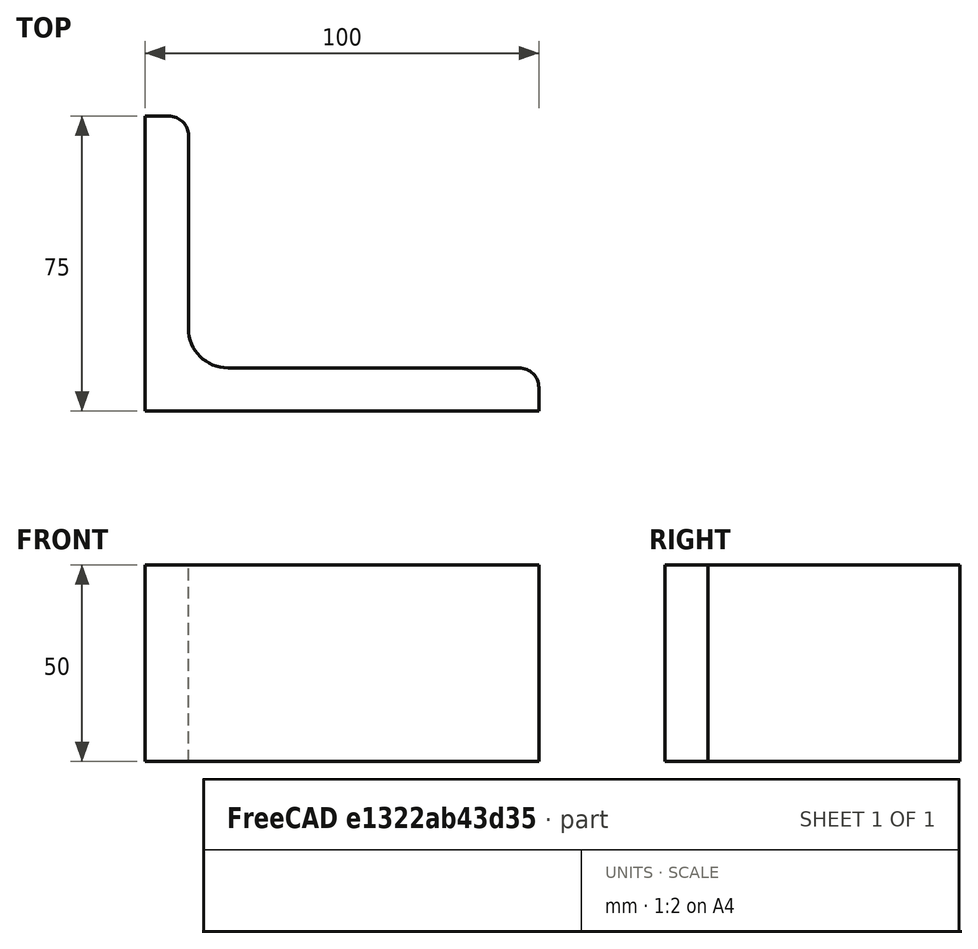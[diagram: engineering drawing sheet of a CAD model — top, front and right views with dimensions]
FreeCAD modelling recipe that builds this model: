
FCSTD DOCUMENT  (FreeCAD 0.15R4671 (Git))
Label: Angle Bar 100x75x11 EN10056 S235JR
License: All rights reserved
LicenseURL: http://en.wikipedia.org/wiki/All_rights_reserved
objects: Sketcher::SketchObject×1, Part::Extrusion×1
note: 2 computed .brp shape members not serialized (recipe doc carries the construction recipe); baked Part::Feature solids carry a one-line shape summary decoded from their .brp

FEATURE [Sketcher::SketchObject] Sketch
  sketch-geometry (9):
    g0: LineSegment StartX=0 StartY=0 StartZ=0 EndX=100 EndY=0 EndZ=0
    g1: LineSegment StartX=100 StartY=0 StartZ=0 EndX=100 EndY=6 EndZ=0
    g2: LineSegment StartX=95 StartY=11 StartZ=0 EndX=21 EndY=11 EndZ=0
    g3: LineSegment StartX=0 StartY=0 StartZ=0 EndX=0 EndY=75 EndZ=0
    g4: LineSegment StartX=0 StartY=75 StartZ=0 EndX=6 EndY=75 EndZ=0
    g5: LineSegment StartX=11 StartY=70 StartZ=0 EndX=11 EndY=21 EndZ=0
    g6: ArcOfCircle CenterX=21 CenterY=21 CenterZ=0 NormalX=0 NormalY=0 NormalZ=1 Radius=10 StartAngle=3.14159 EndAngle=4.71239
    g7: ArcOfCircle CenterX=6 CenterY=70 CenterZ=0 NormalX=0 NormalY=0 NormalZ=1 Radius=5 StartAngle=0 EndAngle=1.5708
    g8: ArcOfCircle CenterX=95 CenterY=6 CenterZ=0 NormalX=0 NormalY=0 NormalZ=1 Radius=5 StartAngle=0 EndAngle=1.5708
  constraints (23):
    c: Coincident(g0,g-1)
    c: Horizontal(g0)
    c: Coincident(g1,g0)
    c: Vertical(g1)
    c: Horizontal(g2)
    c: Coincident(g3,g-1)
    c: Vertical(g3)
    c: Coincident(g4,g3)
    c: Horizontal(g4)
    c: Vertical(g5)
    c: Tangent(g5,g6) = -1.5708
    c: Tangent(g2,g6) = 1.5708
    c: Tangent(g4,g7) = 1.5708
    c: Tangent(g5,g7) = 1.5708
    c: Tangent(g2,g8) = -1.5708
    c: Tangent(g1,g8) = -1.5708
    c: DistanceX(g0) = 100
    c: DistanceY(g3) = 75
    c: DistanceY(g0,g2) = 11
    c: DistanceX(g3,g5) = 11
    c: Radius(g6) = 10
    c: Radius(g8) = 5
    c: Radius(g7) = 5
FEATURE [Part::Extrusion] Extrude  label="Angle Bar 100x75x11 EN10056 S235JR"
  Base = -> Sketch
  Dir = (0,0,50)
  Solid = true
